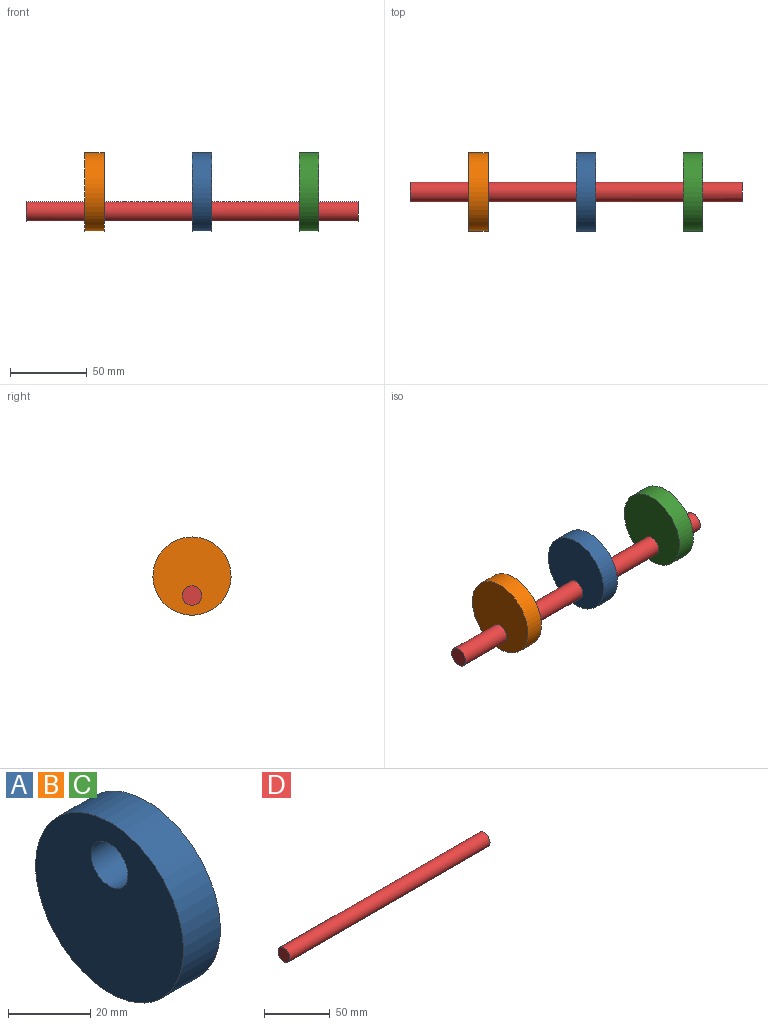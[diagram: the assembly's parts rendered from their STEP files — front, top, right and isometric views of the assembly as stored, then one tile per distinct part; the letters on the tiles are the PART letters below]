
ASSEMBLY  parts=4 mates=3
PART A: 4 faces, bbox 12.7x50.8x50.8 mm
  f0: plane 50.8x50.8mm, normal (1,0,0), area 1900.2mm2, adj f2,f3
  f1: plane 50.8x50.8mm, normal (-1,0,0), area 1900.2mm2, adj f2,f3
  f2: cylinder r=25.4mm len=50.8mm, axis (1,0,0), area 2026.8mm2, adj f0,f1
  f3: cylinder r=6.35mm len=12.7mm, axis (-1,0,0), area 506.7mm2, adj f0,f1
PART B: same geometry as A
PART C: same geometry as A
PART D: 3 faces, bbox 215.9x12.7x12.7 mm
  f0: plane 12.7x12.7mm, normal (1,0,0), area 126.7mm2, adj f1
  f1: cylinder r=6.35mm len=215.9mm, axis (-1,0,0), area 8614mm2, adj f0,f2
  f2: plane 12.7x12.7mm, normal (-1,0,0), area 126.7mm2, adj f1
PLACE A rot(axis=(-1,0,0),180deg) t=(82.55,0,57.15)mm
PLACE B rot(axis=(0,-1,0),180deg) t=(76.2,0,57.15)mm
PLACE C rot(axis=(-1,0,0),180deg) t=(152.4,0,57.15)mm
PLACE D t=(12.7,0,-57.15)mm
MATE fastened D.f1 <-> B.f3  axis (-1,0,0) through (44.45,0,0)mm
MATE fastened A.f3 <-> D.f1  axis (-1,0,0) through (114.3,0,0)mm
MATE fastened C.f3 <-> D.f1  axis (-1,0,0) through (184.15,0,0)mm
